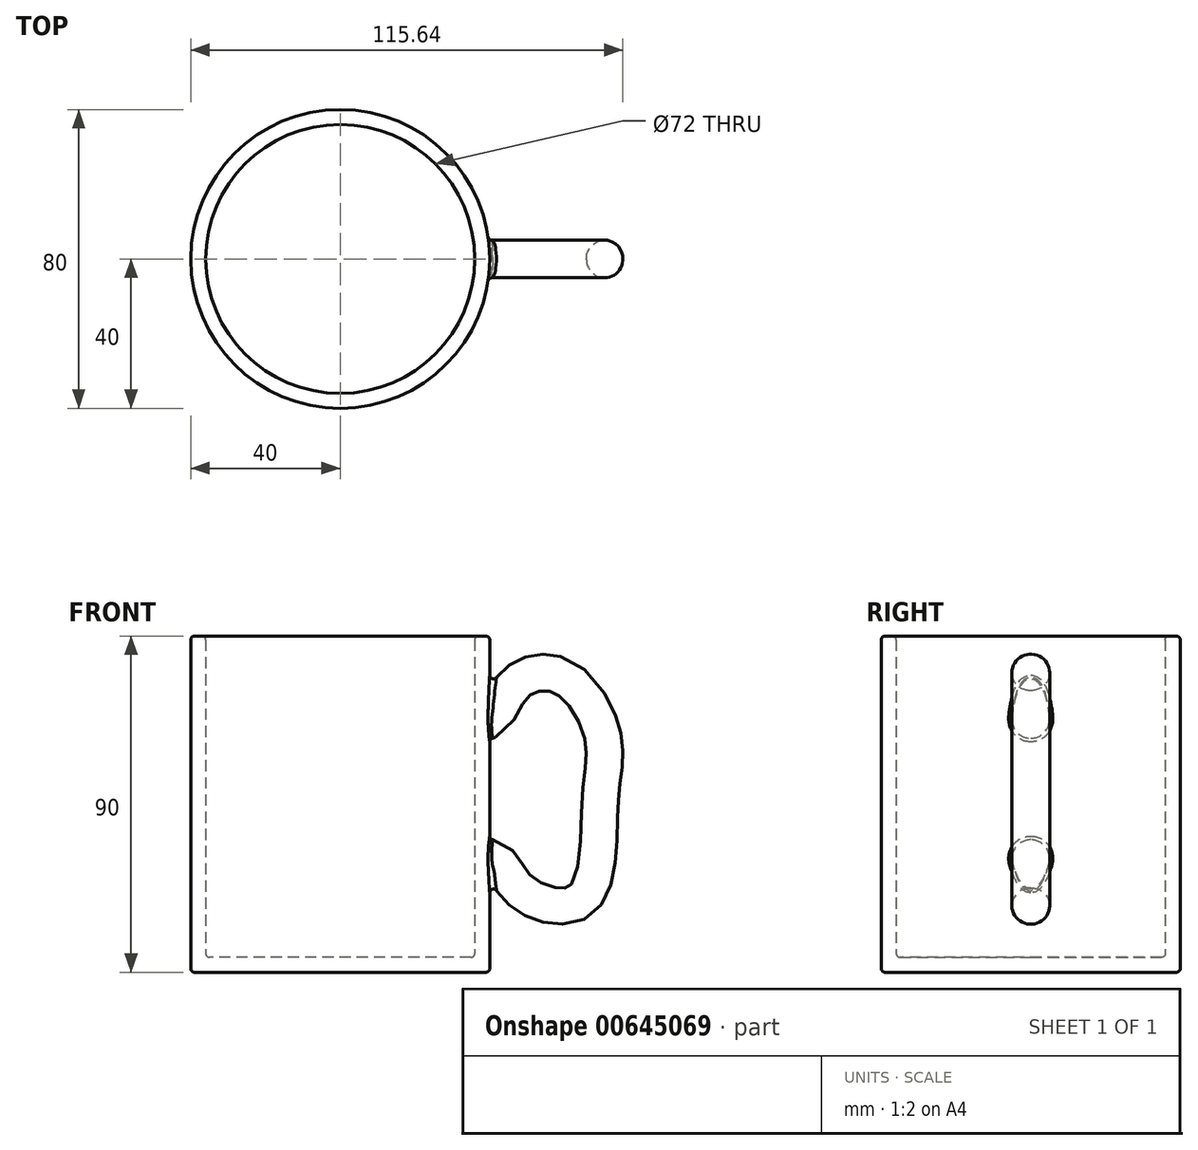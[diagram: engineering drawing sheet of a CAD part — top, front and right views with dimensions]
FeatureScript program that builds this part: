
annotation { "Feature Type Name" : "Feature", "Feature Type Description" : "" }
export const myFeature = defineFeature(function(context is Context, id is Id, definition is map)
    precondition{}
    {
        {
            var Q0;
            Q0=qCreatedBy(makeId("Top.planeOp"),FACE);
            var sketch = newSketch(context, id + "F0", { "sketchPlane" : qUnion([Q0])});
            skCircle(sketch, "E0", {"center": v(0, 0) * mm, "radius": 40 * mm});
            skSolve(sketch);
        }
        {
            var Q0;
            Q0=makeQuery(id+"F0.imprint","IMPRINT",FACE,{"disambiguationData":[TD([[makeQuery(id+"F0.imprint","IMPRINT",EDGE,{"derivedFrom":sQuery(id+"F0.wireOp",EDGE,"E0")}),1.0]])]});
            extrude(context, id + "F1", {"entities" : qUnion([Q0]), "depth" : 90 * mm, "offsetDistance" : 25 * mm});
        }
        {
            var Q0;
            Q0=qCreatedBy(makeId("Right.planeOp"),FACE);
            cPlane(context, id + "F2", {"entities" : qUnion([Q0]), "cplaneType" : CPlaneType.OFFSET, "offset" : 35 * mm, "width" : 150 * mm, "height" : 150 * mm});
        }
        {
            var Q0;
            Q0=qCreatedBy(id+"F2.planeOp",FACE);
            var sketch = newSketch(context, id + "F3", { "sketchPlane" : qUnion([Q0])});
            skCircle(sketch, "E1", {"center": v(0, 67.93) * mm, "radius": 5.05 * mm});
            skSolve(sketch);
        }
        {
            var Q0;
            Q0=qCreatedBy(makeId("Front.planeOp"),FACE);
            var sketch = newSketch(context, id + "F4", { "sketchPlane" : qUnion([Q0])});
            skFitSpline(sketch, "E2", {"points": [v(35.29, 68.22) * mm, v(40.33, 68.22) * mm, v(46.23, 77.07) * mm, v(59.38, 79.53) * mm, v(70.57, 63.43) * mm, v(69.96, 46.34) * mm, v(64.8, 19.3) * mm, v(48.57, 21.14) * mm, v(41.8, 29.37) * mm, v(35.41, 30.48) * mm], "startDerivative": vector(80.25, -21.41) * mm, "endDerivative": vector(-90.65, -3.05) * mm});
            skSolve(sketch);
        }
        {
            var Q0;
            Q0 = qSketchRegion(id + "F3", true);
            var Q1;
            Q1 = qConstructionFilter(qBodyType(qCreatedBy(id + "F4" ,EDGE), BodyType.WIRE), ConstructionObject.NO);
            sweep(context, id + "F5", {"operationType" : NewBodyOperationType.ADD, "profiles" : qUnion([Q0]), "path" : qUnion([Q1])});
        }
        {
            var Q0;
            Q0=makeQuery(id+"F1.opExtrude","CAP_FACE",FACE,{"disambiguationData":[OSD([sQuery(id+"F0.wireOp",EDGE,"E0")])],"isStart":false});
            shell(context, id + "F6", {"entities" : qUnion([Q0]), "thickness" : 4 * mm});
        }
        {
            var Q0;
            Q0=makeQuery(id+"F1.opExtrude","SWEPT_FACE",FACE,{"disambiguationData":[OSD([sQuery(id+"F0.wireOp",EDGE,"E0")])]});
            var Q1;
            Q1=makeQuery(id+"F1.opExtrude","CAP_EDGE",EDGE,{"disambiguationData":[OSD([sQuery(id+"F0.wireOp",EDGE,"E0")])],"isStart":false});
            var Q2;
            Q2=makeQuery(id+"F1.opExtrude","CAP_FACE",FACE,{"disambiguationData":[OSD([sQuery(id+"F0.wireOp",EDGE,"E0")])],"isStart":false});
            var Q3;
            {var subQ0=sQuery(id+"F0.wireOp",EDGE,"E0");Q3=makeQuery(id+"F6.opShell","OFFSET_FACE",FACE,{"disambiguationData":[OSD([subQ0]),TDD([makeQuery(id+"F1.opExtrude","CAP_FACE",FACE,{"disambiguationData":[OSD([subQ0])],"isStart":true})])]});}
            var Q4;
            Q4=makeQuery(id+"F5.opSweep","SWEPT_FACE",FACE,{"disambiguationData":[OSD([sQuery(id+"F3.wireOp",EDGE,"E1"),sQuery(id+"F4.wireOp",EDGE,"E2")])]});
            var Q5;
            Q5=makeQuery(id+"F1.opExtrude","CAP_FACE",FACE,{"disambiguationData":[OSD([sQuery(id+"F0.wireOp",EDGE,"E0")])],"isStart":true});
            var Q6;
            Q6=makeQuery(id+"F1.opExtrude","CAP_EDGE",EDGE,{"disambiguationData":[OSD([sQuery(id+"F0.wireOp",EDGE,"E0")])],"isStart":true});
            fillet(context, id + "F7", {"entities" : qUnion([Q0, Q1, Q2, Q3, Q4, Q5, Q6]), "radius" : 1 * mm, "tangentPropagation" : true, "allowEdgeOverflow" : false});
        }
    });
